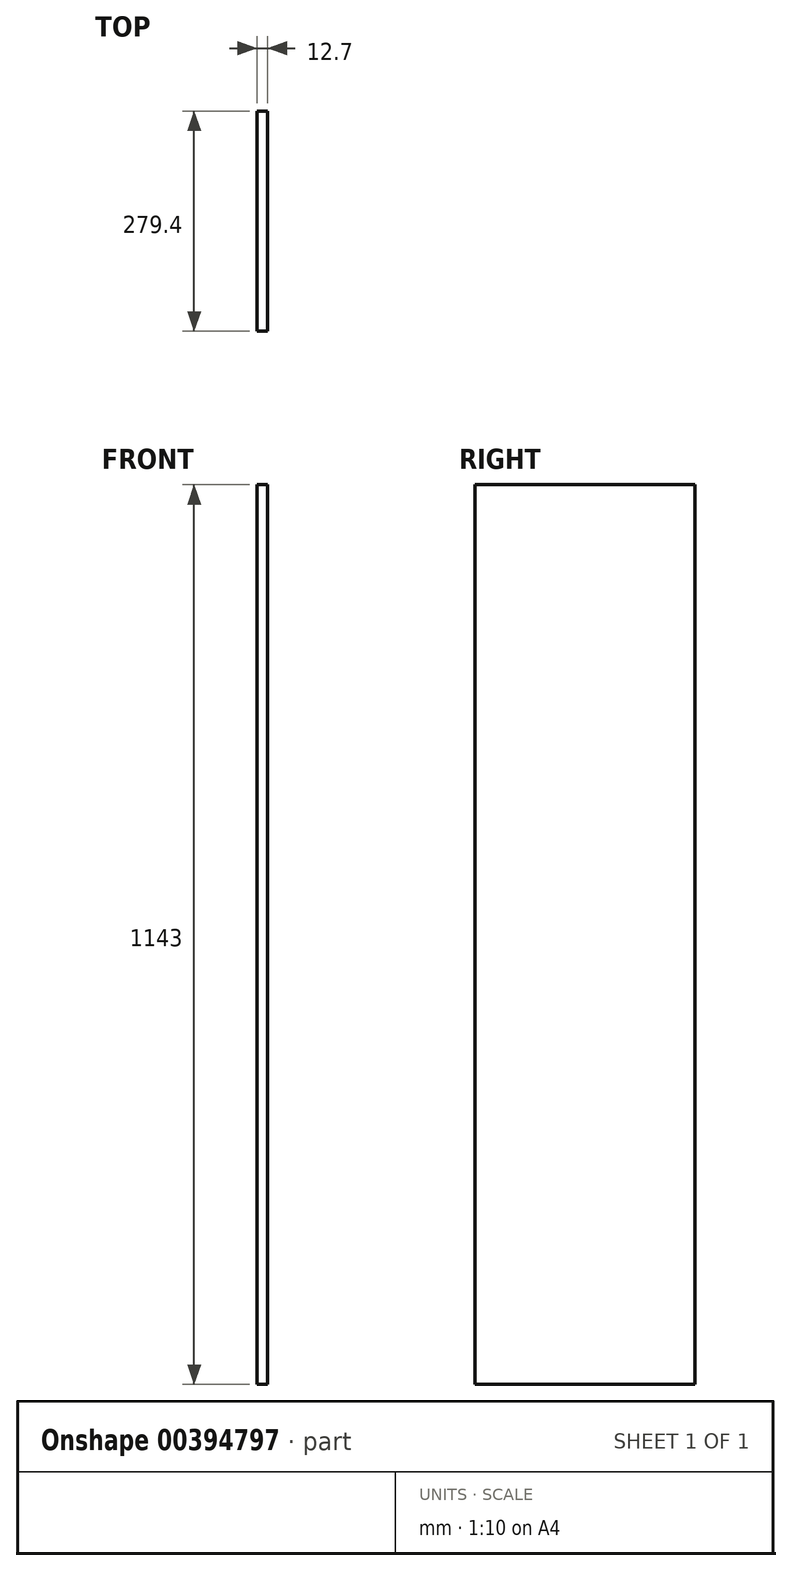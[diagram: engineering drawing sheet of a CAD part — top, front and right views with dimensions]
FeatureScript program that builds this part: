
annotation { "Feature Type Name" : "Feature", "Feature Type Description" : "" }
export const myFeature = defineFeature(function(context is Context, id is Id, definition is map)
    precondition{}
    {
        {
            var Q0;
            Q0=qCreatedBy(makeId("Right.planeOp"),FACE);
            var sketch = newSketch(context, id + "F0", { "sketchPlane" : qUnion([Q0])});
            skLineSegment(sketch, "E0.bottom", {"start": v(-150.68, 675.39) * mm, "end": v(128.72, 675.39) * mm});
            skLineSegment(sketch, "E0.top", {"start": v(-150.68, -467.61) * mm, "end": v(128.72, -467.61) * mm});
            skLineSegment(sketch, "E0.left", {"start": v(-150.68, 675.39) * mm, "end": v(-150.68, -467.61) * mm});
            skLineSegment(sketch, "E0.right", {"start": v(128.72, 675.39) * mm, "end": v(128.72, -467.61) * mm});
            skSolve(sketch);
        }
        {
            var Q0;
            Q0 = qSketchRegion(id + "F0", true);
            extrude(context, id + "F1", {"entities" : qUnion([Q0]), "depth" : 12.7 * mm});
        }
    });
